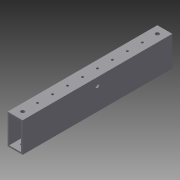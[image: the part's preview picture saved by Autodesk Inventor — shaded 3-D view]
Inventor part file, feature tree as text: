
AUTODESK INVENTOR PART (.ipt)
format: ipt  version: 2015 SP1 (Build 190203100, 203)  size: 137,728 bytes
history: native  units: in
note: dims shown in document units (in); Inventor stores cm internally (conversion verified against a paired STEP export)
features: sketch x4, projected_geometry x3, extrude x2, hole x2, pattern_linear x1
ambient origin geometry x8: Origin, YZ Plane, XZ Plane, XY Plane, X Axis, Y Axis, Z Axis, Center Point
bodies: Solid1 (feature_tree)
feature tree (12):
  extrude  "Extrusion1"  Depth=2.0in
  hole  "Hole1"  [1 undecoded]
  pattern_linear  "Rectangular Pattern1"  Spacing1=10.0in  [1 undecoded]
  extrude  "Extrusion2"  Depth=1.0in
  hole  "Hole2"  [1 undecoded]
  sketch  "Sketch1"  dims[d0=1.0in d1=2.0in]
  sketch  "Sketch2"  dims[d2=0.8in d3=1.8in]
  projected_geometry  "Projected Loop1"
  sketch  "Sketch3"  dims[d4=0.1in]
  projected_geometry  "Projected Loop2"
  sketch  "Sketch4"  dims[d5=0.1in d6=10.0in d7=0.0in d8=0.5in d9=0.5in d10=0.1562in d11=0.75in d12=0.375in d13=0.25in d14=0.5635in d15=1.0in d16=0.8108in d17=3.937in d19=1.0in d20=0.25in d21=0.25in d22=11.0in d23=0.0in d24=0.5in d25=5.0in d26=0.25in d27=0.75in d28=0.375in d29=0.25in d30=0.5635in d31=1.0in d32=0.8108in]
  projected_geometry  "Projected Loop3"
note: 3 required parameter values undecoded (feature->parameter linkage not recoverable at this tier; creation-order binding heuristic only, values carry confidence <= 0.55)
